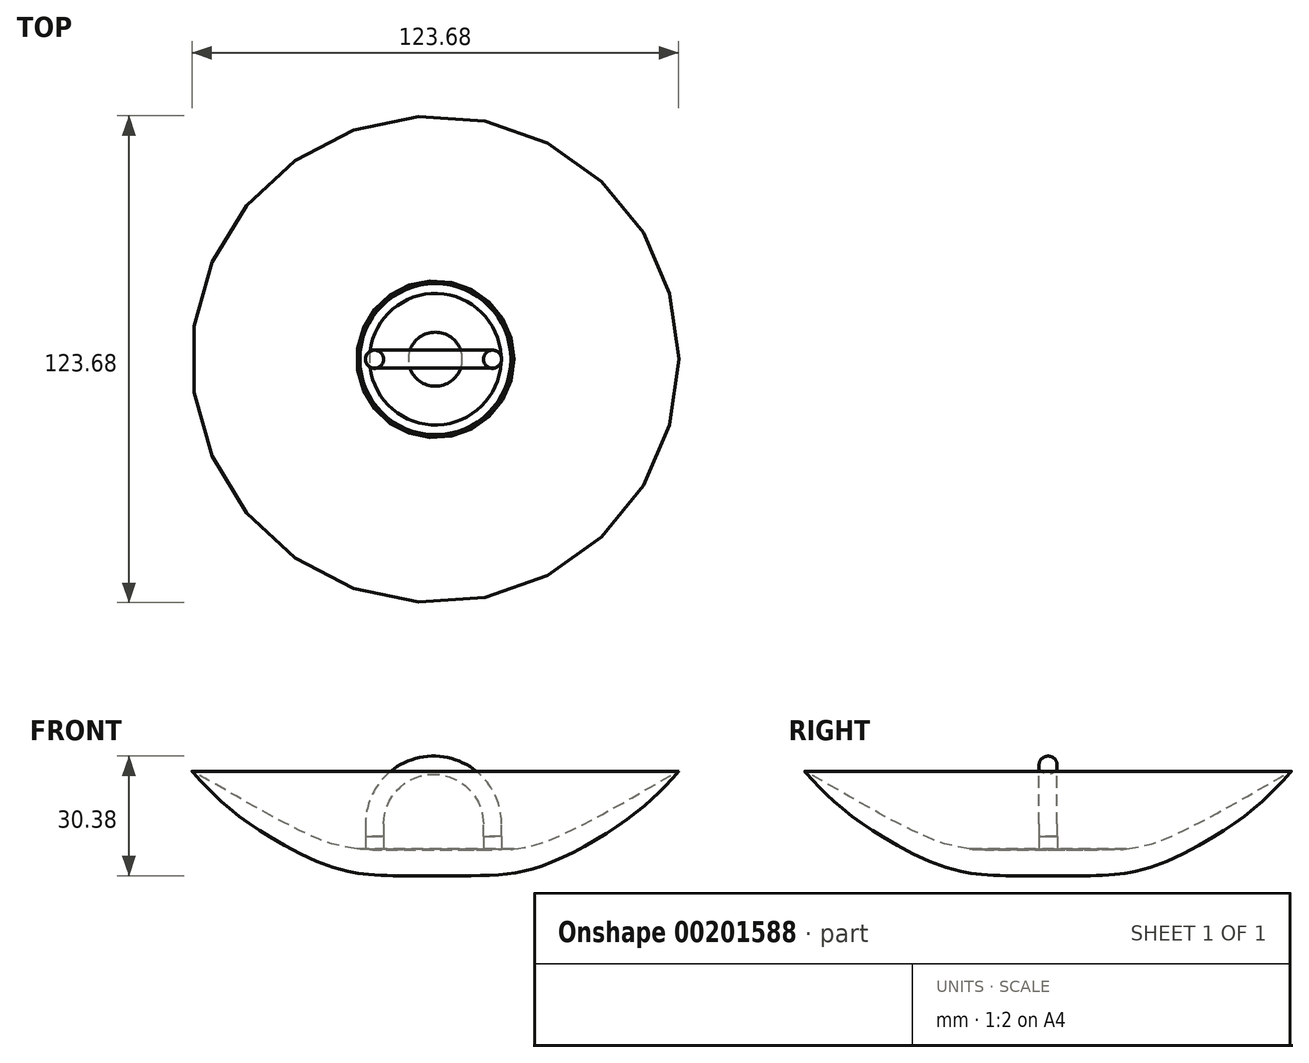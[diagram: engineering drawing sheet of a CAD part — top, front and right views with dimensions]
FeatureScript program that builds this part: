
annotation { "Feature Type Name" : "Feature", "Feature Type Description" : "" }
export const myFeature = defineFeature(function(context is Context, id is Id, definition is map)
    precondition{}
    {
        {
            var Q0;
            Q0=qCreatedBy(makeId("Front.planeOp"),FACE);
            var sketch = newSketch(context, id + "F0", { "sketchPlane" : qUnion([Q0])});
            skFitSpline(sketch, "E0", {"points": [v(0, 0) * mm, v(15.42, 0) * mm, v(29.05, 3.03) * mm, v(50.77, 15.65) * mm, v(61.84, 26.33) * mm], "startDerivative": vector(67.58, -1.92) * mm, "endDerivative": vector(39.93, 44.22) * mm});
            skLineSegment(sketch, "E1", {"start": v(0, 6.45) * mm, "end": v(0, 0) * mm});
            skPoint(sketch, "E2.orphan", {"position": v(0, 26.33) * mm});
            skFitSpline(sketch, "E3", {"points": [v(6.86, 6.45) * mm, v(16.7, 6.45) * mm, v(32.1, 10.2) * mm, v(61.84, 26.33) * mm, v(61.47, 25.92) * mm], "startDerivative": vector(43.4, -0.53) * mm, "endDerivative": vector(-12.23, -10.95) * mm});
            skLineSegment(sketch, "E4", {"start": v(0, 6.45) * mm, "end": v(19.18, 6.45) * mm});
            skFitSpline(sketch, "E5", {"points": [v(19.18, 6.45) * mm, v(24.62, 8) * mm, v(34.87, 12.92) * mm, v(48.3, 20.15) * mm, v(60, 27.8) * mm, v(64.53, 31.9) * mm], "startDerivative": vector(33.99, 7.7) * mm, "endDerivative": vector(24.95, 24.82) * mm});
            skFitSpline(sketch, "E6", {"points": [v(61.84, 26.33) * mm, v(62.34, 26.99) * mm, v(62.96, 28.1) * mm, v(63.63, 29.4) * mm, v(64.24, 30.72) * mm, v(64.53, 31.9) * mm], "startDerivative": vector(3.04, 3.69) * mm, "endDerivative": vector(1.12, 5.9) * mm});
            skSolve(sketch);
        }
        {
            var Q0;
            Q0=makeQuery(id+"F0.imprint","IMPRINT",FACE,{"disambiguationData":[TD([[makeQuery(id+"F0.imprint","IMPRINT",EDGE,{"derivedFrom":sQuery(id+"F0.wireOp",EDGE,"E0")}),1.0]])]});
            var Q1;
            Q1=sQuery(id+"F0.wireOp",EDGE,"E1");
            revolve(context, id + "F1", {"entities" : qUnion([Q0]), "axis" : qUnion([Q1]), "revolveType" : RevolveType.FULL});
        }
        {
            var Q0;
            Q0=makeQuery(id+"F1.opRevolve","SWEPT_FACE",FACE,{"disambiguationData":[OSD([sQuery(id+"F0.wireOp",EDGE,"E4")])]});
            var sketch = newSketch(context, id + "F2", { "sketchPlane" : qUnion([Q0])});
            skCircle(sketch, "E7", {"center": v(14.52, 0) * mm, "radius": 2.32 * mm});
            skCircle(sketch, "E8", {"center": v(-15.43, 0) * mm, "radius": 2.32 * mm});
            skSolve(sketch);
        }
        {
            var Q0;
            Q0=makeQuery(id+"F2.imprint","IMPRINT",FACE,{"disambiguationData":[TD([[makeQuery(id+"F2.imprint","IMPRINT",EDGE,{"derivedFrom":sQuery(id+"F2.wireOp",EDGE,"E7")}),1.0]])]});
            var Q1;
            Q1=makeQuery(id+"F2.imprint","IMPRINT",FACE,{"disambiguationData":[TD([[makeQuery(id+"F2.imprint","IMPRINT",EDGE,{"derivedFrom":sQuery(id+"F2.wireOp",EDGE,"E8")}),1.0]])]});
            extrude(context, id + "F3", {"entities" : qUnion([Q0, Q1]), "operationType" : NewBodyOperationType.ADD, "depth" : 3.3 * mm});
        }
        {
            var Q0;
            Q0=qCreatedBy(makeId("Front.planeOp"),FACE);
            var sketch = newSketch(context, id + "F4", { "sketchPlane" : qUnion([Q0])});
            skLineSegment(sketch, "E9.0", {"start": v(-17.75, 9.76) * mm, "end": v(-13.1, 9.76) * mm});
            skLineSegment(sketch, "E10.0", {"start": v(12.2, 9.76) * mm, "end": v(16.84, 9.76) * mm});
            skLineSegment(sketch, "E11", {"start": v(-13.1, 9.76) * mm, "end": v(-13.1, 12.93) * mm});
            skLineSegment(sketch, "E12", {"start": v(12.2, 9.76) * mm, "end": v(12.2, 12.93) * mm});
            skArc(sketch, "E13", {"start": v(12.2, 12.93) * mm, "mid": v(-0.46, 25.58) * mm, "end": v(-13.1, 12.93) * mm});
            skSolve(sketch);
        }
        {
            var Q0;
            Q0=makeQuery(id+"F3.opExtrude","CAP_FACE",FACE,{"disambiguationData":[OSD([sQuery(id+"F2.wireOp",EDGE,"E7")])],"isStart":false});
            var sketch = newSketch(context, id + "F5", { "sketchPlane" : qUnion([Q0])});
            skCircle(sketch, "E14", {"center": v(14.52, 0) * mm, "radius": 2.3 * mm});
            skSolve(sketch);
        }
        {
            var Q0;
            Q0=makeQuery(id+"F5.imprint","IMPRINT",FACE,{"disambiguationData":[TD([[makeQuery(id+"F5.imprint","IMPRINT",EDGE,{"derivedFrom":sQuery(id+"F5.wireOp",EDGE,"E14")}),1.0]])]});
            var Q1;
            Q1=sQuery(id+"F4.wireOp",EDGE,"E13");
            var Q2;
            Q2=sQuery(id+"F4.wireOp",EDGE,"E11");
            var Q3;
            Q3=sQuery(id+"F4.wireOp",EDGE,"E12");
            sweep(context, id + "F6", {"operationType" : NewBodyOperationType.ADD, "profiles" : qUnion([Q0]), "path" : qUnion([Q1, Q2, Q3])});
        }
    });
